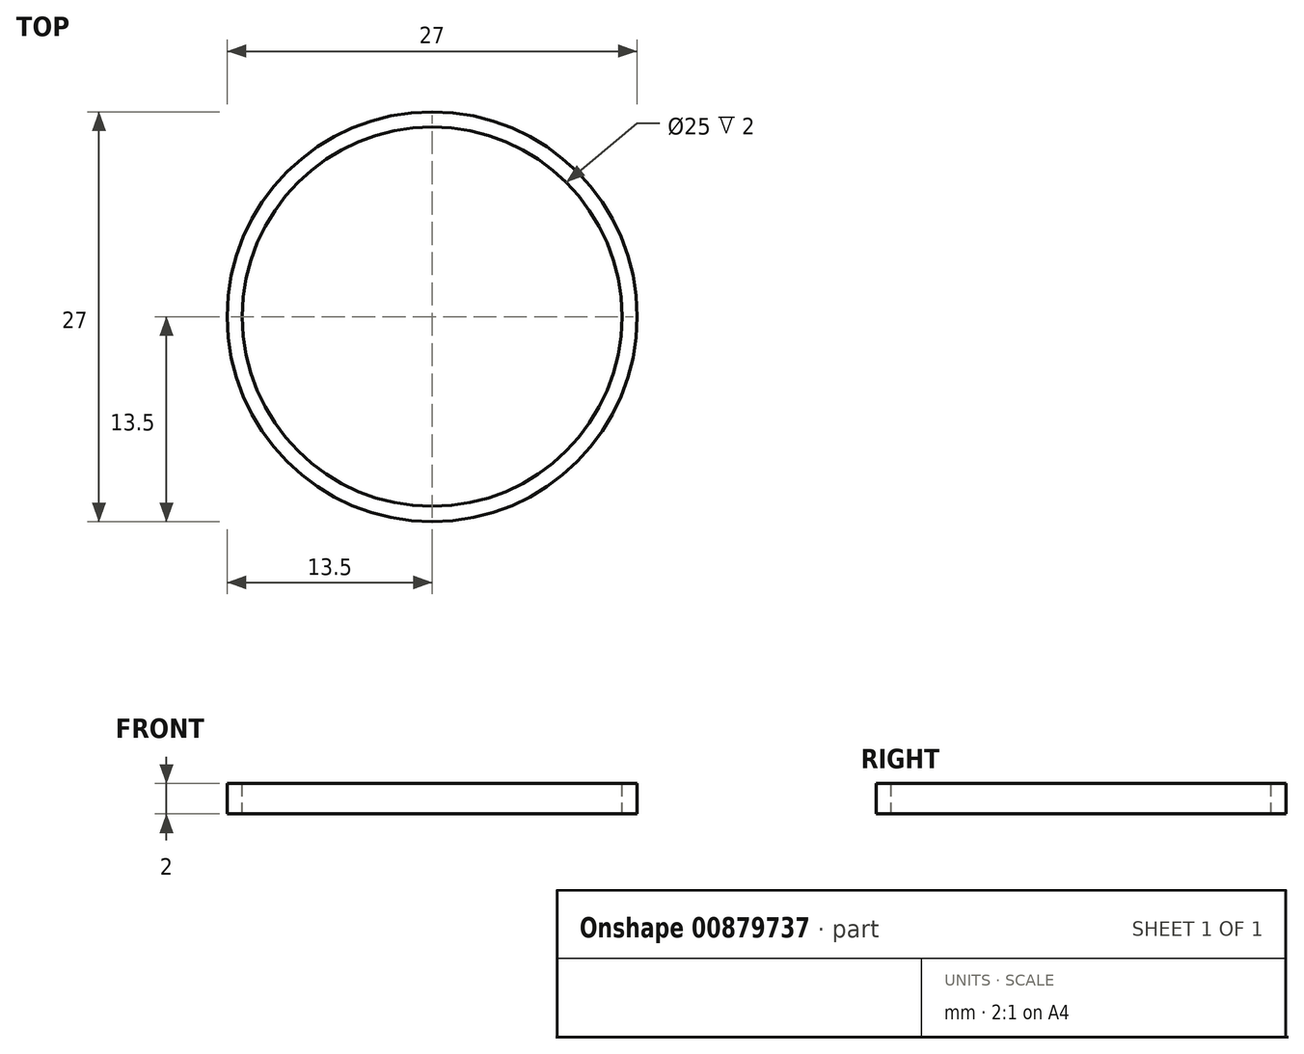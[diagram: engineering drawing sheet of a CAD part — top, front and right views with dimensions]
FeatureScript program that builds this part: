
annotation { "Feature Type Name" : "Feature", "Feature Type Description" : "" }
export const myFeature = defineFeature(function(context is Context, id is Id, definition is map)
    precondition{}
    {
        {
            var Q0;
            Q0=qCreatedBy(makeId("Top.planeOp"),FACE);
            var sketch = newSketch(context, id + "F0", { "sketchPlane" : qUnion([Q0])});
            skCircle(sketch, "E0", {"center": v(0, 0) * mm, "radius": 13.5 * mm});
            skSolve(sketch);
        }
        {
            var Q0;
            Q0=makeQuery(id+"F0.imprint","IMPRINT",FACE,{"disambiguationData":[TD([[makeQuery(id+"F0.imprint","IMPRINT",EDGE,{"derivedFrom":sQuery(id+"F0.wireOp",EDGE,"E0")}),1.0]])]});
            extrude(context, id + "F1", {"entities" : qUnion([Q0]), "depth" : 2 * mm, "offsetDistance" : 25 * mm});
        }
        {
            var Q0;
            Q0=makeQuery(id+"F1.opExtrude","CAP_FACE",FACE,{"disambiguationData":[OSD([sQuery(id+"F0.wireOp",EDGE,"E0")])],"isStart":false});
            cPlane(context, id + "F2", {"entities" : qUnion([Q0]), "cplaneType" : CPlaneType.OFFSET, "offset" : 0 * mm, "width" : 150 * mm, "height" : 150 * mm});
        }
        {
            var Q0;
            Q0=qCreatedBy(id+"F2.planeOp",FACE);
            var sketch = newSketch(context, id + "F3", { "sketchPlane" : qUnion([Q0])});
            skCircle(sketch, "E1", {"center": v(0, 0) * mm, "radius": 12.5 * mm});
            skSolve(sketch);
        }
        {
            var Q0;
            Q0=makeQuery(id+"F3.imprint","IMPRINT",FACE,{"disambiguationData":[TD([[makeQuery(id+"F3.imprint","IMPRINT",EDGE,{"derivedFrom":sQuery(id+"F3.wireOp",EDGE,"E1")}),1.0]])]});
            extrude(context, id + "F4", {"entities" : qUnion([Q0]), "operationType" : NewBodyOperationType.REMOVE, "oppositeDirection" : true, "depth" : 25 * mm, "offsetDistance" : 25 * mm});
        }
    });
